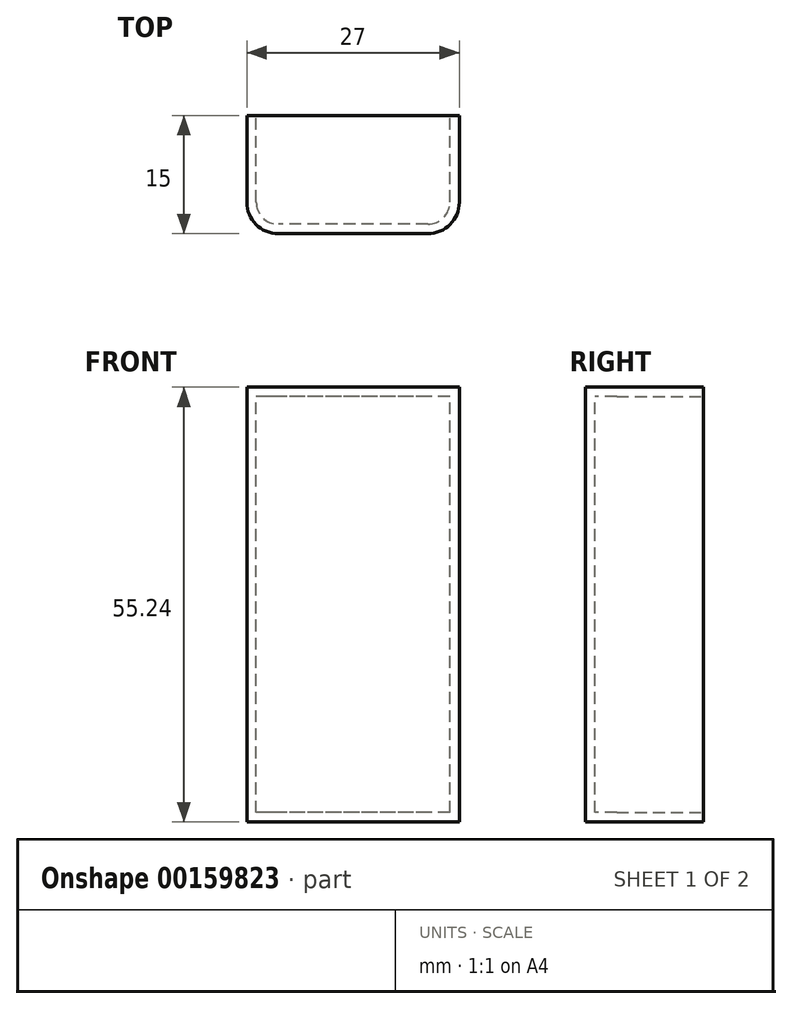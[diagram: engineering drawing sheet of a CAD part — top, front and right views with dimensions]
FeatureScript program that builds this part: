
annotation { "Feature Type Name" : "Feature", "Feature Type Description" : "" }
export const myFeature = defineFeature(function(context is Context, id is Id, definition is map)
    precondition{}
    {
        {
            var Q0;
            Q0=qCreatedBy(makeId("Front.planeOp"),FACE);
            var sketch = newSketch(context, id + "F0", { "sketchPlane" : qUnion([Q0])});
            skLineSegment(sketch, "E0.bottom", {"start": v(13.5, -27.62) * mm, "end": v(-13.5, -27.62) * mm});
            skLineSegment(sketch, "E0.top", {"start": v(13.5, 27.63) * mm, "end": v(-13.5, 27.63) * mm});
            skLineSegment(sketch, "E0.left", {"start": v(13.5, -27.62) * mm, "end": v(13.5, 27.63) * mm});
            skLineSegment(sketch, "E0.right", {"start": v(-13.5, -27.63) * mm, "end": v(-13.5, 27.63) * mm});
            skPoint(sketch, "E0.middle", {"position": v(0, 0) * mm});
            skSolve(sketch);
        }
        {
            var Q0;
            Q0=makeQuery(id+"F0.imprint","IMPRINT",FACE,{"disambiguationData":[TD([[makeQuery(id+"F0.imprint","IMPRINT",EDGE,{"derivedFrom":sQuery(id+"F0.wireOp",EDGE,"E0.bottom")}),-1.0]])]});
            extrude(context, id + "F1", {"entities" : qUnion([Q0]), "depth" : 15 * mm});
        }
        {
            var Q0;
            Q0=makeQuery(id+"F1.opExtrude","CAP_EDGE",EDGE,{"disambiguationData":[OSD([sQuery(id+"F0.wireOp",EDGE,"E0.left")])],"isStart":false});
            var Q1;
            Q1=makeQuery(id+"F1.opExtrude","CAP_EDGE",EDGE,{"disambiguationData":[OSD([sQuery(id+"F0.wireOp",EDGE,"E0.right")])],"isStart":false});
            fillet(context, id + "F2", {"entities" : qUnion([Q0, Q1]), "radius" : 4 * mm, "tangentPropagation" : true, "allowEdgeOverflow" : false});
        }
        {
            var Q0;
            Q0=makeQuery(id+"F1.opExtrude","CAP_FACE",FACE,{"disambiguationData":[OSD([sQuery(id+"F0.wireOp",EDGE,"E0.bottom"),sQuery(id+"F0.wireOp",EDGE,"E0.top"),sQuery(id+"F0.wireOp",EDGE,"E0.left"),sQuery(id+"F0.wireOp",EDGE,"E0.right")])],"isStart":true});
            shell(context, id + "F3", {"entities" : qUnion([Q0]), "thickness" : 1.2 * mm});
        }
    });
